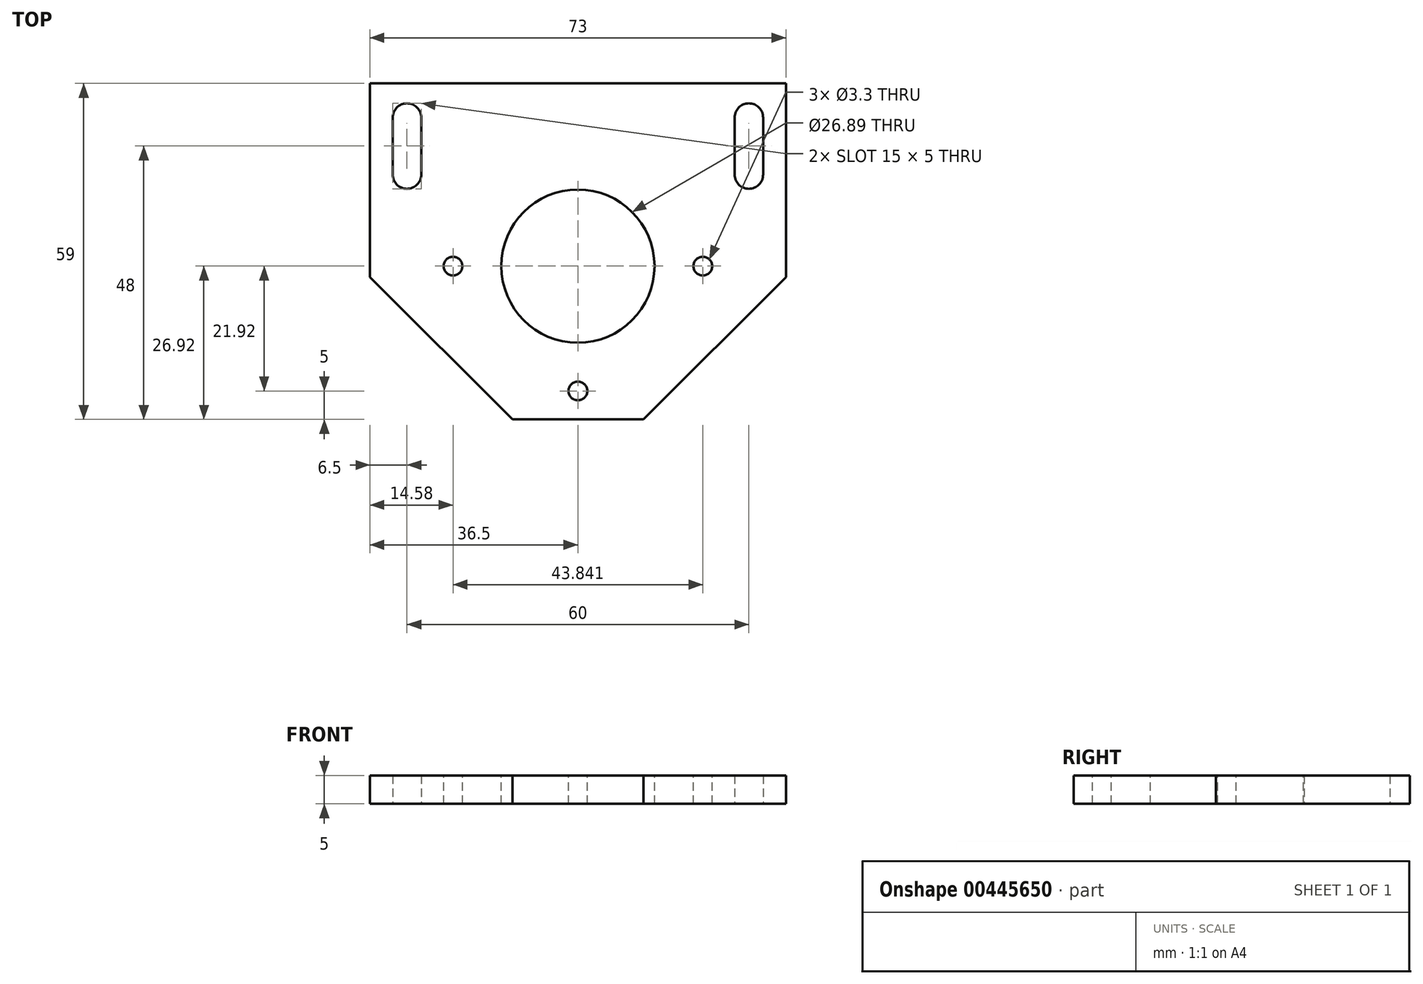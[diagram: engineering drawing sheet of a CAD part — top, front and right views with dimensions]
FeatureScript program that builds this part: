
annotation { "Feature Type Name" : "Feature", "Feature Type Description" : "" }
export const myFeature = defineFeature(function(context is Context, id is Id, definition is map)
    precondition{}
    {
        {
            var Q0;
            Q0=qCreatedBy(makeId("Top.planeOp"),FACE);
            var sketch = newSketch(context, id + "F0", { "sketchPlane" : qUnion([Q0])});
            skLineSegment(sketch, "E0.bottom", {"start": v(-36.5, -29.5) * mm, "end": v(36.5, -29.5) * mm});
            skLineSegment(sketch, "E0.top", {"start": v(-36.5, 29.5) * mm, "end": v(36.5, 29.5) * mm});
            skLineSegment(sketch, "E0.left", {"start": v(-36.5, -29.5) * mm, "end": v(-36.5, 29.5) * mm});
            skLineSegment(sketch, "E0.right", {"start": v(36.5, -29.5) * mm, "end": v(36.5, 29.5) * mm});
            skPoint(sketch, "E0.middle", {"position": v(0, 0) * mm});
            skLineSegment(sketch, "E1", {"start": v(-30, 23.5) * mm, "end": v(-30, 13.5) * mm});
            skLineSegment(sketch, "E2.1.0.0", {"start": v(30, 23.5) * mm, "end": v(30, 13.5) * mm});
            skLineSegment(sketch, "E2.direction1", {"start": v(-30, 13.5) * mm, "end": v(30, 13.5) * mm, "construction": true});
            skArc(sketch, "E3.0.startCap", {"start": v(-32.5, 23.5) * mm, "mid": v(-30, 26) * mm, "end": v(-27.5, 23.5) * mm});
            skArc(sketch, "E3.0.endCap", {"start": v(-27.5, 13.5) * mm, "mid": v(-30, 11) * mm, "end": v(-32.5, 13.5) * mm});
            skLineSegment(sketch, "E3.0.left", {"start": v(-27.5, 23.5) * mm, "end": v(-27.5, 13.5) * mm});
            skLineSegment(sketch, "E3.0.right", {"start": v(-32.5, 23.5) * mm, "end": v(-32.5, 13.5) * mm});
            skArc(sketch, "E3.1.startCap", {"start": v(27.5, 23.5) * mm, "mid": v(30, 26) * mm, "end": v(32.5, 23.5) * mm});
            skArc(sketch, "E3.1.endCap", {"start": v(32.5, 13.5) * mm, "mid": v(30, 11) * mm, "end": v(27.5, 13.5) * mm});
            skLineSegment(sketch, "E3.1.left", {"start": v(32.5, 23.5) * mm, "end": v(32.5, 13.5) * mm});
            skLineSegment(sketch, "E3.1.right", {"start": v(27.5, 23.5) * mm, "end": v(27.5, 13.5) * mm});
            skSolve(sketch);
        }
        {
            var Q0;
            Q0=qSketchRegion(id+"F0",true);
            extrude(context, id + "F1", {"entities" : qUnion([Q0]), "depth" : 5 * mm});
        }
        {
            var Q0;
            Q0=makeQuery(id+"F1.opExtrude","SWEPT_EDGE",EDGE,{"disambiguationData":[OSD([sQuery(id+"F0.wireOp",EDGE,"E0.bottom"),sQuery(id+"F0.wireOp",EDGE,"E0.left")])]});
            var Q1;
            Q1=makeQuery(id+"F1.opExtrude","SWEPT_EDGE",EDGE,{"disambiguationData":[OSD([sQuery(id+"F0.wireOp",EDGE,"E0.bottom"),sQuery(id+"F0.wireOp",EDGE,"E0.right")])]});
            chamfer(context, id + "F2", {"entities" : qUnion([Q0, Q1]), "width" : 25 * mm, "tangentPropagation" : true});
        }
        {
            var Q0;
            Q0=makeQuery(id+"F1.opExtrude","CAP_FACE",FACE,{"disambiguationData":[OSD([sQuery(id+"F0.wireOp",EDGE,"E0.bottom"),sQuery(id+"F0.wireOp",EDGE,"E0.top"),sQuery(id+"F0.wireOp",EDGE,"E0.left"),sQuery(id+"F0.wireOp",EDGE,"E0.right"),sQuery(id+"F0.wireOp",EDGE,"E3.0.startCap"),sQuery(id+"F0.wireOp",EDGE,"E3.0.endCap"),sQuery(id+"F0.wireOp",EDGE,"E3.0.left"),sQuery(id+"F0.wireOp",EDGE,"E3.0.right"),sQuery(id+"F0.wireOp",EDGE,"E3.1.startCap"),sQuery(id+"F0.wireOp",EDGE,"E3.1.endCap"),sQuery(id+"F0.wireOp",EDGE,"E3.1.left"),sQuery(id+"F0.wireOp",EDGE,"E3.1.right")])],"isStart":false});
            var sketch = newSketch(context, id + "F3", { "sketchPlane" : qUnion([Q0])});
            skPoint(sketch, "E4", {"position": v(0, -24.5) * mm});
            skLineSegment(sketch, "E5", {"start": v(0, -24.5) * mm, "end": v(-21.92, -2.58) * mm, "construction": true});
            skLineSegment(sketch, "E6", {"start": v(0, -24.5) * mm, "end": v(-61.13, -24.5) * mm, "construction": true});
            skLineSegment(sketch, "E7.MirrorCS", {"start": v(0, -24.5) * mm, "end": v(21.92, -2.58) * mm, "construction": true});
            skPoint(sketch, "E8", {"position": v(-21.92, -2.58) * mm});
            skPoint(sketch, "E9", {"position": v(21.92, -2.58) * mm});
            skCircle(sketch, "E10", {"center": v(0, -2.58) * mm, "radius": 13.45 * mm});
            skSolve(sketch);
        }
        {
            var Q0;
            Q0=sQuery(id+"F3.wireOp",VERTEX,"E8");
            var Q1;
            Q1=sQuery(id+"F3.wireOp",VERTEX,"E4");
            var Q2;
            Q2=sQuery(id+"F3.wireOp",VERTEX,"E9");
            var Q3;
            Q3=makeQuery(id+"F1.opExtrude","SWEPT_BODY",BODY,{"disambiguationData":[OSD([sQuery(id+"F0.wireOp",EDGE,"E0.bottom"),sQuery(id+"F0.wireOp",EDGE,"E0.top"),sQuery(id+"F0.wireOp",EDGE,"E0.left"),sQuery(id+"F0.wireOp",EDGE,"E0.right"),sQuery(id+"F0.wireOp",EDGE,"E3.0.startCap"),sQuery(id+"F0.wireOp",EDGE,"E3.0.endCap"),sQuery(id+"F0.wireOp",EDGE,"E3.0.left"),sQuery(id+"F0.wireOp",EDGE,"E3.0.right"),sQuery(id+"F0.wireOp",EDGE,"E3.1.startCap"),sQuery(id+"F0.wireOp",EDGE,"E3.1.endCap"),sQuery(id+"F0.wireOp",EDGE,"E3.1.left"),sQuery(id+"F0.wireOp",EDGE,"E3.1.right")])]});
            hole(context, id + "F4", {"style" : HoleStyle.SIMPLE, "endStyle" : HoleEndStyle.BLIND, "standardTappedOrClearance" : lookupTablePath({ "standard" : "ISO", "fit" : "Normal", "size" : "M3", "type" : "Clearance" }), "standardBlindInLast" : lookupTablePath({ "fit" : "Standard", "standard" : "ISO", "size" : "M3", "type" : "Clearance" }), "holeDiameter" : 3.3 * mm, "holeDepth" : 13.8 * mm, "tappedDepth" : 12 * mm, "tapClearance" : 3, "locations" : qUnion([Q0, Q1, Q2]), "scope" : qUnion([Q3])});
        }
        {
            var Q0;
            Q0=qSketchRegion(id+"F3",true);
            extrude(context, id + "F5", {"entities" : qUnion([Q0]), "operationType" : NewBodyOperationType.REMOVE, "endBound" : BoundingType.UP_TO_NEXT, "oppositeDirection" : true, "depth" : 25 * mm});
        }
    });
